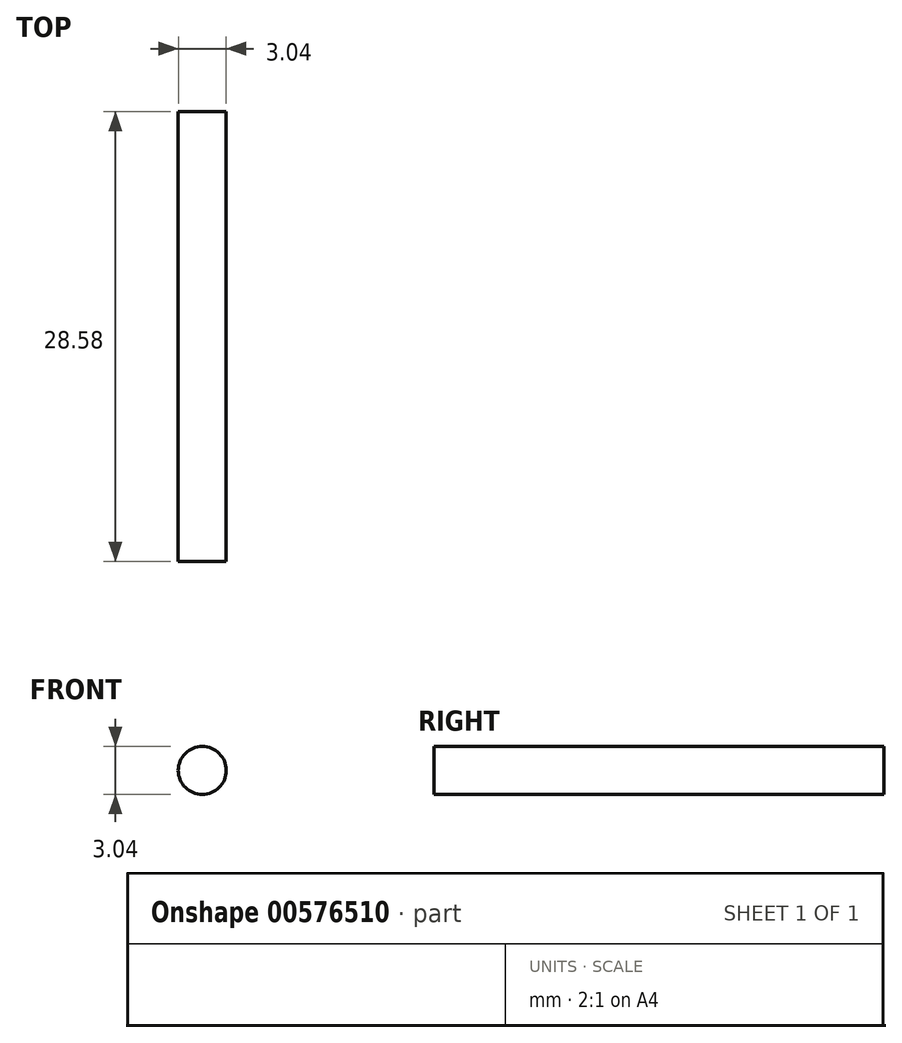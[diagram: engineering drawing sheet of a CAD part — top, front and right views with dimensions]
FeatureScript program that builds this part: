
annotation { "Feature Type Name" : "Feature", "Feature Type Description" : "" }
export const myFeature = defineFeature(function(context is Context, id is Id, definition is map)
    precondition{}
    {
        {
            var Q0;
            Q0=qCreatedBy(makeId("Front.planeOp"),FACE);
            var sketch = newSketch(context, id + "F0", { "sketchPlane" : qUnion([Q0])});
            skCircle(sketch, "E0", {"center": v(0, 0) * mm, "radius": 1.52 * mm});
            skPoint(sketch, "E1", {"position": v(1.52, 0) * mm});
            skSolve(sketch);
        }
        {
            var Q0;
            Q0=makeQuery(id+"F0.imprint","IMPRINT",FACE,{"disambiguationData":[TD([[makeQuery(id+"F0.imprint","IMPRINT",EDGE,{"derivedFrom":sQuery(id+"F0.wireOp",EDGE,"E0")}),1.0]])]});
            extrude(context, id + "F1", {"entities" : qUnion([Q0]), "depth" : 28.57 * mm, "offsetDistance" : 25.4 * mm});
        }
    });
